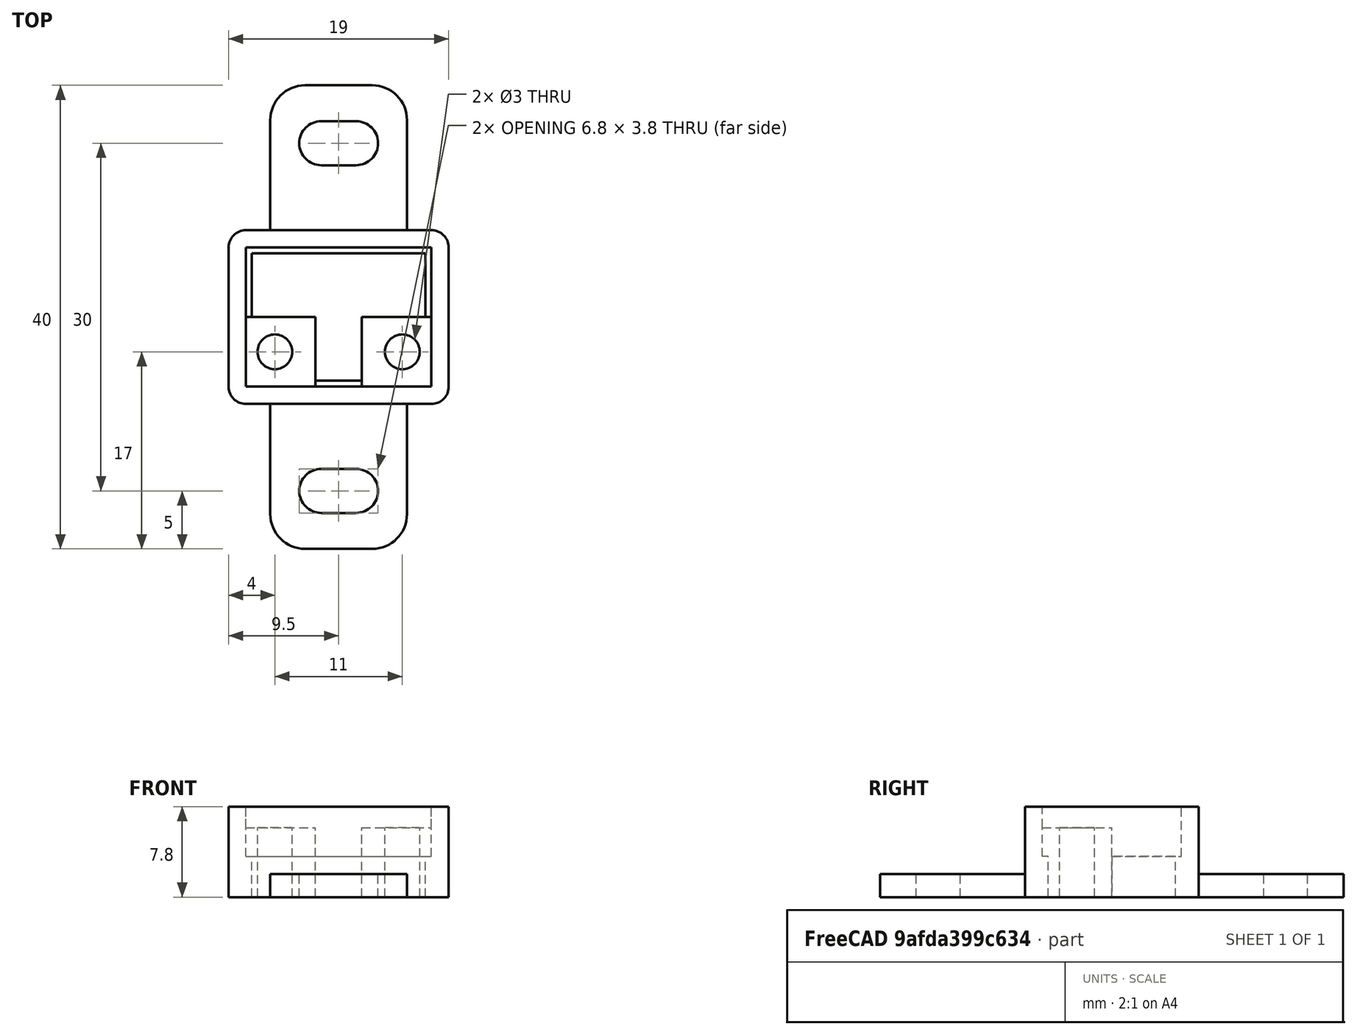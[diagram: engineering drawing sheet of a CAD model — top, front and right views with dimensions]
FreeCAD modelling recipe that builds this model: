
FCSTD DOCUMENT  (FreeCAD 0.19R)
Label: bmx280
License: All rights reserved
LicenseURL: http://en.wikipedia.org/wiki/All_rights_reserved
objects: Part::Box×4, Part::MultiFuse×3, Part::FeaturePython×2, Part::Cut×2, Spreadsheet::Sheet×1, Part::Cylinder×1, Part::Fillet×1, Part::Feature×1, App::Part×1
note: 14 computed .brp shape members not serialized (recipe doc carries the construction recipe); baked Part::Feature solids carry a one-line shape summary decoded from their .brp

FEATURE [Spreadsheet::Sheet] Spreadsheet  label="p"
  cells = A1=hole_x_dist; B1(hole_x_dist)=11; A2=hole_y_off; B2(hole_y_off)=3; A3=pcb_under; B3(pcb_under)=3; A4=pcb_x; B4(pcb_x)=16; A5=pcb_y; B5(pcb_y)=12; A6=hole_stand_x; B6(hole_stand_x)=6; A7=hole_stand_y; B7(hole_stand_y)=6; A8=hole_r; B8(hole_r)=1.5; A9=box_wall; B9(box_wall)=1.5; A10=under_layer; B10(under_layer)=3; A11=pcb_height; B11(pcb_height)=1.8; A12=under_pcb_border; B12(under_pcb_border)=0.5
FEATURE [Part::Box] Box  label="bottom cube"
  AttacherType = Attacher::AttachEngine3D
  Height = 7.8
  Length = 19
  Width = 15
  expr: Height = <<p>>.pcb_under + <<p>>.pcb_height + <<p>>.under_layer
  expr: Length = <<p>>.pcb_x + <<p>>.box_wall * 2
  expr: Width = <<p>>.pcb_y + <<p>>.box_wall * 2
FEATURE [Part::Box] Box001  label="bottom extraction"
  AttacherType = Attacher::AttachEngine3D
  Height = 10
  Length = 15
  Placement = pos=(2,2,0) rot=(0,0,1;0rad)
  Width = 11
  expr: Width = <<p>>.pcb_y - <<p>>.under_pcb_border * 2
  expr: Length = <<p>>.pcb_x - <<p>>.under_pcb_border * 2
  expr: .Placement.Base.x = <<p>>.under_pcb_border + <<p>>.box_wall
  expr: .Placement.Base.y = <<p>>.under_pcb_border + <<p>>.box_wall
FEATURE [Part::Box] Box002  label="pcb extraction"
  AttacherType = Attacher::AttachEngine3D
  Height = 10
  Length = 16
  Placement = pos=(1.5,1.5,3.5) rot=(0,0,1;0rad)
  Width = 12
  expr: Width = <<p>>.pcb_y
  expr: Length = <<p>>.pcb_x
  expr: .Placement.Base.x = <<p>>.box_wall
  expr: .Placement.Base.y = <<p>>.box_wall
  expr: .Placement.Base.z = <<p>>.under_pcb_border + <<p>>.under_layer
FEATURE [Part::MultiFuse] Fusion  label="bottom extraction001"
  Shapes = -> [Box001,Box002]
FEATURE [Part::Box] Box003  label="hole stand cube"
  AttacherType = Attacher::AttachEngine3D
  Height = 6
  Length = 6
  Placement = pos=(1.5,1.5,0) rot=(0,0,1;0rad)
  Width = 6
  expr: Length = <<p>>.hole_stand_x
  expr: Width = <<p>>.hole_stand_y
  expr: Height = <<p>>.pcb_under + <<p>>.under_layer
  expr: .Placement.Base.x = <<p>>.box_wall
  expr: .Placement.Base.y = <<p>>.box_wall
FEATURE [Part::FeaturePython] Array  label="hole stand array"  # Draft array (typed FeaturePython)
  Angle = 360
  ArrayType = 0
  Axis = (0,0,1)
  Base = -> Box003
  Center = (0,0,0)
  Fuse = false
  IntervalAxis = (0,0,0)
  IntervalX = (10,0,0)
  IntervalY = (0,6,0)
  IntervalZ = (0,0,1)
  NumberPolar = 1
  NumberX = 2
  NumberY = 1
  NumberZ = 1
  expr: .IntervalX.x = <<p>>.pcb_x - <<p>>.hole_stand_x
  expr: .IntervalY.y = <<p>>.pcb_y - <<p>>.hole_stand_y
FEATURE [Part::Cylinder] Cylinder  label="pcb hole"
  Angle = 360
  AttacherType = Attacher::AttachEngine3D
  Height = 10
  Placement = pos=(4,4.5,0) rot=(0,0,1;0rad)
  Radius = 1.5
  expr: Radius = <<p>>.hole_r
  expr: .Placement.Base.x = (<<p>>.box_wall * 2 + <<p>>.pcb_x - <<p>>.hole_x_dist) / 2
FEATURE [Part::FeaturePython] Array001  label="hole array"  # Draft array (typed FeaturePython)
  Angle = 360
  ArrayType = 0
  Axis = (0,0,1)
  Base = -> Cylinder
  Center = (0,0,0)
  Fuse = false
  IntervalAxis = (0,0,0)
  IntervalX = (11,0,0)
  IntervalY = (0,3,0)
  IntervalZ = (0,0,1)
  NumberPolar = 1
  NumberX = 2
  NumberY = 1
  NumberZ = 1
  expr: .IntervalX.x = <<p>>.hole_x_dist
  expr: .IntervalY.y = Spreadsheet.hole_y_off
FEATURE [Part::Fillet] Fillet001  label="bottom cube fillet"
  Base = -> Box
  Edges = 4 edges r=1.5: [Edge1,Edge3,Edge5,Edge7]
FEATURE [Part::Feature] Cut002001  label="attach plane y dir001"
  Placement = pos=(3.6,-12.5,0) rot=(0,0,1;0rad)
  shape: bbox 11.8 x 40 x 2 mm, 20 faces (baked)
FEATURE [Part::MultiFuse] Fusion002  label="bottom fusion"
  Shapes = -> [Fillet001,Cut002001]
FEATURE [Part::Cut] Cut  label="pcb box cut"
  Base = -> Fusion002
  Tool = -> Fusion
FEATURE [Part::MultiFuse] Fusion001  label="frame fusion"
  Shapes = -> [Array,Cut]
FEATURE [Part::Cut] Cut001  label="frame fusion with holes"
  Base = -> Fusion001
  Tool = -> Array001
FEATURE [App::Part] Part  label="body part"
  Group = -> [Fusion,Fusion002,Box002,Box003,Box001,Array001,Cut,Array,Cylinder,Fusion001,Cut001]
  Origin = -> Origin
